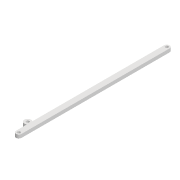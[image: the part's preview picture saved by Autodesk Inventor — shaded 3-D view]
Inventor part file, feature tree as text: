
AUTODESK INVENTOR PART (.ipt)
format: ipt  version: 2022 (Build 260153000, 153)  size: 95,232 bytes
history: native  units: mm
features: extrude x1, sketch x1
ambient origin geometry x8: Origin, YZ Plane, XZ Plane, XY Plane, X Axis, Y Axis, Z Axis, Center Point
bodies: Solid1 (feature_tree)
feature tree (2):
  extrude  "Extrusion1"  Depth=8.0mm
  sketch  "Sketch1"  dims[d0=215.0mm d1=8.0mm d2=4.2mm d3=4.2mm d4=5.0mm d5=0.0mm d6=4.2mm d7=10.0mm d8=3.0mm d9=20.0mm]
